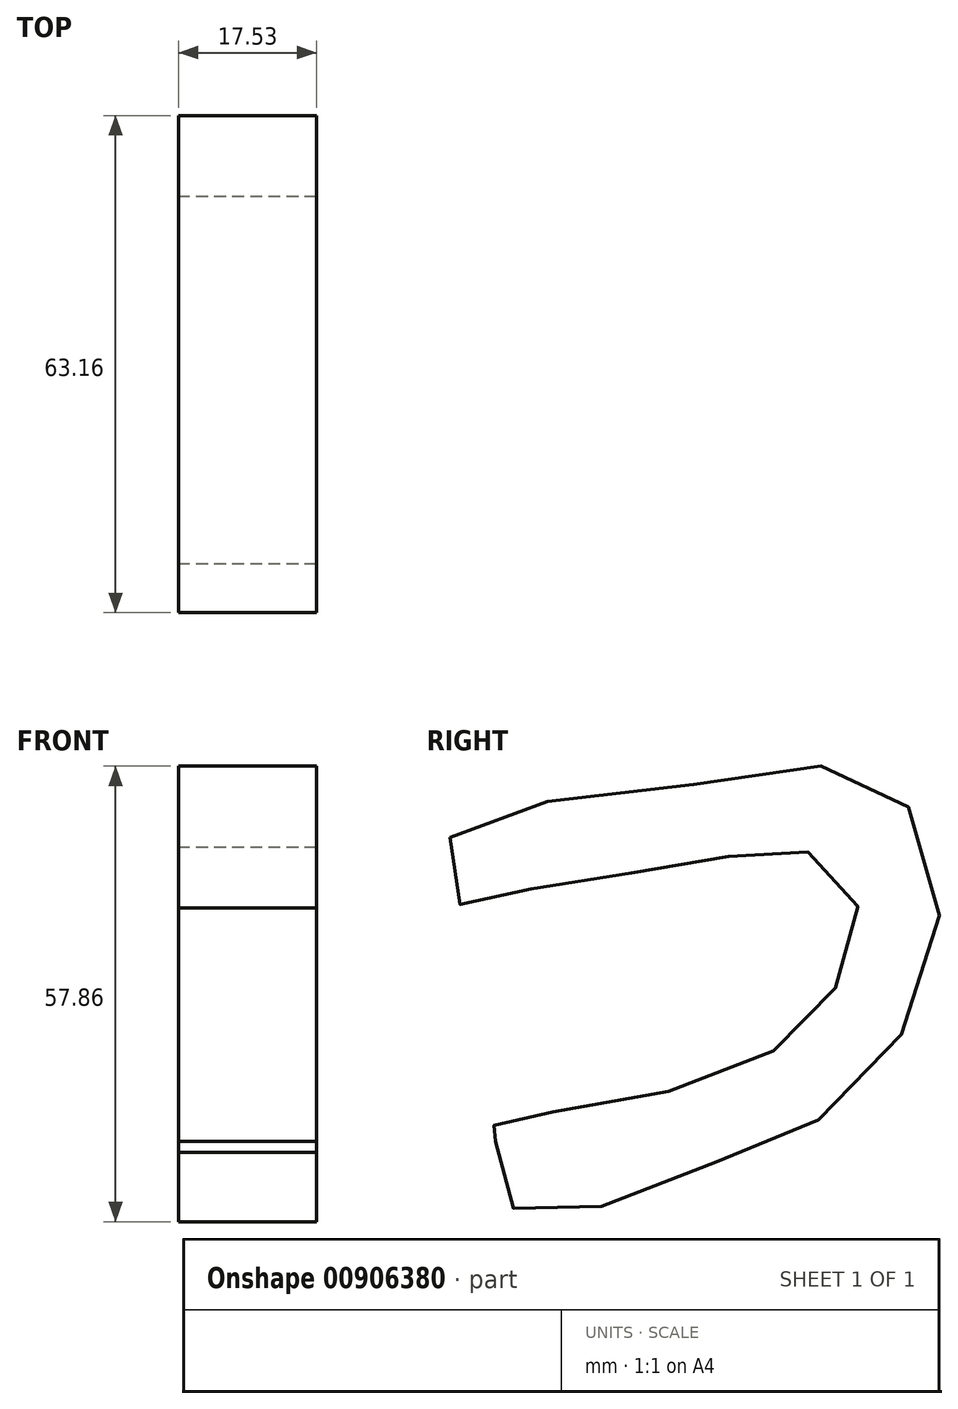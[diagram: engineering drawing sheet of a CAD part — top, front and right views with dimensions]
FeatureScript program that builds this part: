
annotation { "Feature Type Name" : "Feature", "Feature Type Description" : "" }
export const myFeature = defineFeature(function(context is Context, id is Id, definition is map)
    precondition{}
    {
        {
            var Q0;
            Q0=qCreatedBy(makeId("Right.planeOp"),FACE);
            var sketch = newSketch(context, id + "F0", { "sketchPlane" : qUnion([Q0])});
            skFitSpline(sketch, "E0", {"points": [v(16.72, 20) * mm, v(43.57, 26.09) * mm, v(70.6, 27.7) * mm, v(78.84, 8.94) * mm, v(65.46, -14.58) * mm, v(43.64, -23.57) * mm, v(25.06, -27.44) * mm, v(22.48, -18.58) * mm, v(22.08, -19.94) * mm, v(22.39, -16.34) * mm, v(28.23, -14.9) * mm, v(52.66, -9.6) * mm, v(65.13, 0) * mm, v(68.25, 12.4) * mm, v(60.36, 18.64) * mm, v(46.95, 16.4) * mm, v(27.83, 13.73) * mm, v(17.95, 11.53) * mm, v(16.72, 20) * mm]});
            skSolve(sketch);
        }
        {
            var Q0;
            Q0 = qSketchRegion(id + "F0", true);
            extrude(context, id + "F1", {"entities" : qUnion([Q0]), "depth" : 17.53 * mm, "offsetDistance" : 25.4 * mm});
        }
    });
